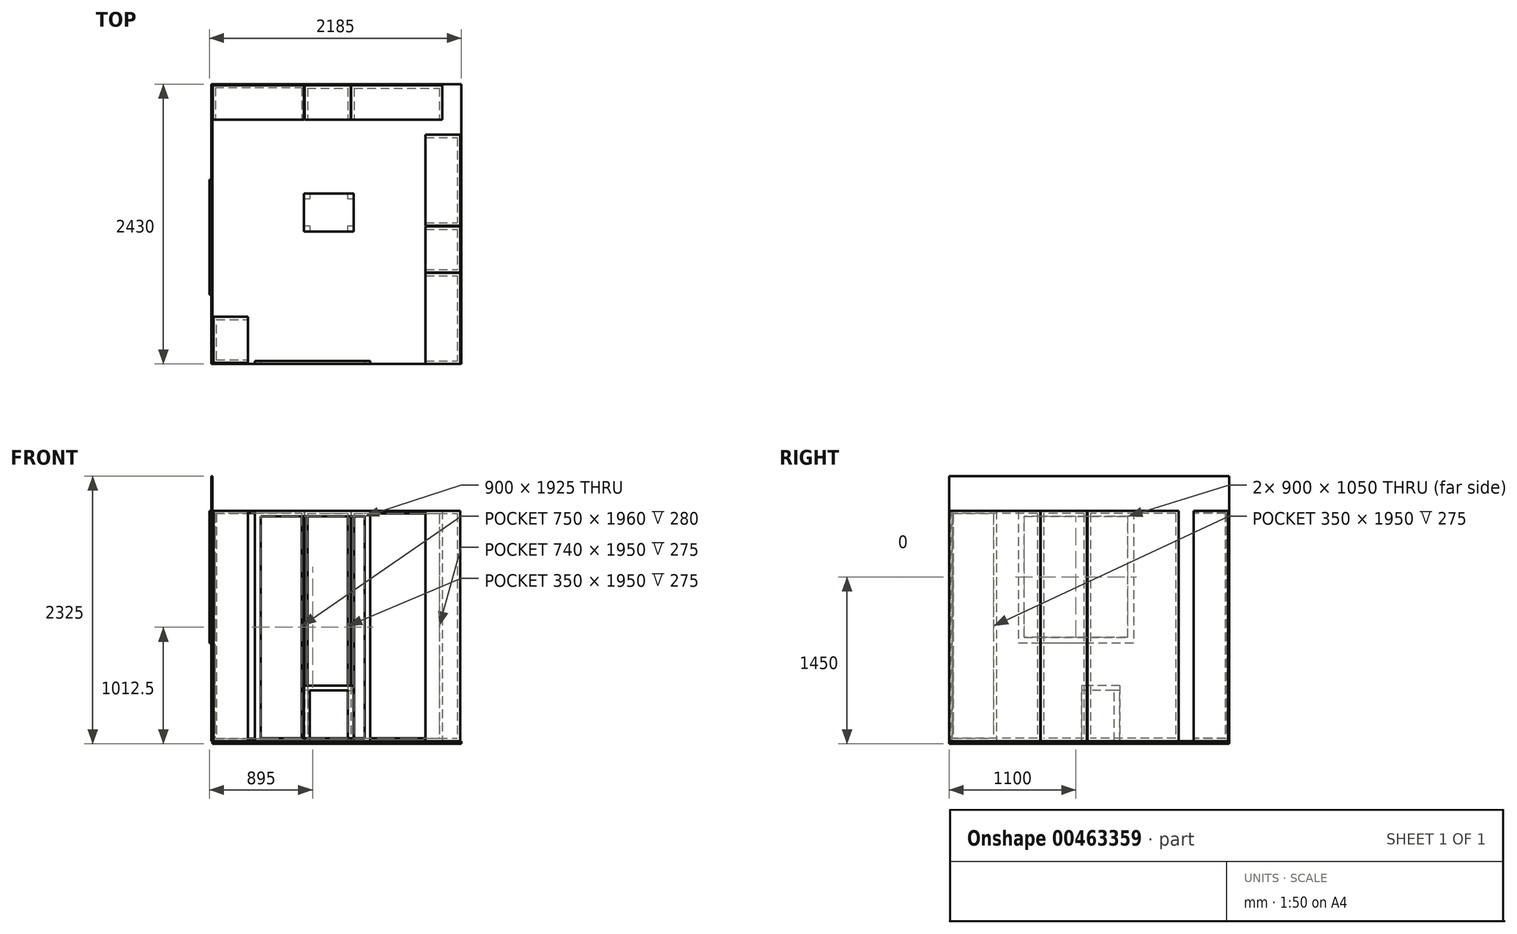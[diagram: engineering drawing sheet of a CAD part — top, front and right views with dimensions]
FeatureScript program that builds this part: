
annotation { "Feature Type Name" : "Feature", "Feature Type Description" : "" }
export const myFeature = defineFeature(function(context is Context, id is Id, definition is map)
    precondition{}
    {
        {
            var Q0;
            Q0=qCreatedBy(makeId("Top.planeOp"),FACE);
            var sketch = newSketch(context, id + "F0", { "sketchPlane" : qUnion([Q0])});
            skLineSegment(sketch, "E0.bottom", {"start": v(0, 0) * mm, "end": v(2160, 0) * mm});
            skLineSegment(sketch, "E0.top", {"start": v(0, 2430) * mm, "end": v(2160, 2430) * mm});
            skLineSegment(sketch, "E0.left", {"start": v(0, 0) * mm, "end": v(0, 2430) * mm});
            skLineSegment(sketch, "E0.right", {"start": v(2160, 0) * mm, "end": v(2160, 2430) * mm});
            skSolve(sketch);
        }
        {
            var Q0;
            Q0=qCreatedBy(makeId("Top.planeOp"),FACE);
            var sketch = newSketch(context, id + "F1", { "sketchPlane" : qUnion([Q0])});
            skLineSegment(sketch, "E1.bottom", {"start": v(1850, 1990) * mm, "end": v(2150, 1990) * mm});
            skLineSegment(sketch, "E1.top", {"start": v(1850, 1200) * mm, "end": v(2150, 1200) * mm});
            skLineSegment(sketch, "E1.left", {"start": v(1850, 1990) * mm, "end": v(1850, 1200) * mm});
            skLineSegment(sketch, "E1.right", {"start": v(2150, 1990) * mm, "end": v(2150, 1200) * mm});
            skPoint(sketch, "E2", {"position": v(1850, 1990) * mm});
            skSolve(sketch);
        }
        {
            var Q0;
            Q0=qCreatedBy(makeId("Top.planeOp"),FACE);
            var sketch = newSketch(context, id + "F2", { "sketchPlane" : qUnion([Q0])});
            skLineSegment(sketch, "E3.bottom", {"start": v(800, 2420) * mm, "end": v(1200, 2420) * mm});
            skLineSegment(sketch, "E3.top", {"start": v(800, 2120) * mm, "end": v(1200, 2120) * mm});
            skLineSegment(sketch, "E3.left", {"start": v(800, 2420) * mm, "end": v(800, 2120) * mm});
            skLineSegment(sketch, "E3.right", {"start": v(1200, 2420) * mm, "end": v(1200, 2120) * mm});
            skSolve(sketch);
        }
        {
            var Q0;
            Q0=qCreatedBy(makeId("Top.planeOp"),FACE);
            var sketch = newSketch(context, id + "F3", { "sketchPlane" : qUnion([Q0])});
            skLineSegment(sketch, "E4.bottom", {"start": v(5, 2420) * mm, "end": v(795, 2420) * mm});
            skLineSegment(sketch, "E4.top", {"start": v(5, 2120) * mm, "end": v(795, 2120) * mm});
            skLineSegment(sketch, "E4.left", {"start": v(5, 2420) * mm, "end": v(5, 2120) * mm});
            skLineSegment(sketch, "E4.right", {"start": v(795, 2420) * mm, "end": v(795, 2120) * mm});
            skSolve(sketch);
        }
        {
            var Q0;
            Q0 = qSketchRegion(id + "F3", true);
            extrude(context, id + "F4", {"entities" : qUnion([Q0]), "depth" : 2000 * mm});
        }
        {
            var Q0;
            Q0 = qSketchRegion(id + "F2", true);
            extrude(context, id + "F5", {"entities" : qUnion([Q0]), "depth" : 2000 * mm});
        }
        {
            var Q0;
            Q0 = qSketchRegion(id + "F1", true);
            extrude(context, id + "F6", {"entities" : qUnion([Q0]), "depth" : 2000 * mm});
        }
        {
            var Q0;
            Q0=qCreatedBy(makeId("Top.planeOp"),FACE);
            var sketch = newSketch(context, id + "F7", { "sketchPlane" : qUnion([Q0])});
            skLineSegment(sketch, "E5.bottom", {"start": v(1850, 1195) * mm, "end": v(2150, 1195) * mm});
            skLineSegment(sketch, "E5.top", {"start": v(1850, 795) * mm, "end": v(2150, 795) * mm});
            skLineSegment(sketch, "E5.left", {"start": v(1850, 1195) * mm, "end": v(1850, 795) * mm});
            skLineSegment(sketch, "E5.right", {"start": v(2150, 1195) * mm, "end": v(2150, 795) * mm});
            skSolve(sketch);
        }
        {
            var Q0;
            Q0 = qSketchRegion(id + "F7", true);
            extrude(context, id + "F8", {"entities" : qUnion([Q0]), "depth" : 2000 * mm});
        }
        {
            var Q0;
            Q0=qCreatedBy(makeId("Top.planeOp"),FACE);
            var sketch = newSketch(context, id + "F9", { "sketchPlane" : qUnion([Q0])});
            skLineSegment(sketch, "E6.bottom", {"start": v(1850, 790) * mm, "end": v(2150, 790) * mm});
            skLineSegment(sketch, "E6.top", {"start": v(1850, 0) * mm, "end": v(2150, 0) * mm});
            skLineSegment(sketch, "E6.left", {"start": v(1850, 790) * mm, "end": v(1850, 0) * mm});
            skLineSegment(sketch, "E6.right", {"start": v(2150, 790) * mm, "end": v(2150, 0) * mm});
            skSolve(sketch);
        }
        {
            var Q0;
            Q0 = qSketchRegion(id + "F9", true);
            extrude(context, id + "F10", {"entities" : qUnion([Q0]), "depth" : 2000 * mm});
        }
        {
            var Q0;
            Q0=makeQuery(id+"F4.opExtrude","SWEPT_FACE",FACE,{"disambiguationData":[OSD([sQuery(id+"F3.wireOp",EDGE,"E4.top")])]});
            shell(context, id + "F11", {"entities" : qUnion([Q0]), "thickness" : 20 * mm});
        }
        {
            var Q0;
            Q0=makeQuery(id+"F5.opExtrude","SWEPT_FACE",FACE,{"disambiguationData":[OSD([sQuery(id+"F2.wireOp",EDGE,"E3.top")])]});
            shell(context, id + "F12", {"entities" : qUnion([Q0]), "thickness" : 25 * mm});
        }
        {
            var Q0;
            Q0=qCreatedBy(makeId("Top.planeOp"),FACE);
            var sketch = newSketch(context, id + "F13", { "sketchPlane" : qUnion([Q0])});
            skLineSegment(sketch, "E7.bottom", {"start": v(10, 10) * mm, "end": v(310, 10) * mm});
            skLineSegment(sketch, "E7.top", {"start": v(10, 410) * mm, "end": v(310, 410) * mm});
            skLineSegment(sketch, "E7.left", {"start": v(10, 10) * mm, "end": v(10, 410) * mm});
            skLineSegment(sketch, "E7.right", {"start": v(310, 10) * mm, "end": v(310, 410) * mm});
            skSolve(sketch);
        }
        {
            var Q0;
            Q0 = qSketchRegion(id + "F13", true);
            extrude(context, id + "F14", {"entities" : qUnion([Q0]), "depth" : 2000 * mm});
        }
        {
            var Q0;
            Q0=makeQuery(id+"F14.opExtrude","SWEPT_FACE",FACE,{"disambiguationData":[OSD([sQuery(id+"F13.wireOp",EDGE,"E7.right")])]});
            shell(context, id + "F15", {"entities" : qUnion([Q0]), "thickness" : 25 * mm});
        }
        {
            var Q0;
            Q0=qCreatedBy(makeId("Front.planeOp"),FACE);
            var sketch = newSketch(context, id + "F16", { "sketchPlane" : qUnion([Q0])});
            skLineSegment(sketch, "E8.bottom", {"start": v(1370, 0) * mm, "end": v(370, 0) * mm});
            skLineSegment(sketch, "E8.top", {"start": v(1370, 2000) * mm, "end": v(370, 2000) * mm});
            skLineSegment(sketch, "E8.left", {"start": v(1370, 0) * mm, "end": v(1370, 2000) * mm});
            skLineSegment(sketch, "E8.right", {"start": v(370, 0) * mm, "end": v(370, 2000) * mm});
            skSolve(sketch);
        }
        {
            var Q0;
            Q0=makeQuery(id+"F0.imprint","IMPRINT",FACE,{"disambiguationData":[TD([[makeQuery(id+"F0.imprint","IMPRINT",EDGE,{"derivedFrom":sQuery(id+"F0.wireOp",EDGE,"E0.bottom")}),1.0]])]});
            var sketch = newSketch(context, id + "F17", { "sketchPlane" : qUnion([Q0])});
            skLineSegment(sketch, "E9.bottom", {"start": v(0, 2430) * mm, "end": v(-10, 2430) * mm});
            skLineSegment(sketch, "E9.top", {"start": v(0, 0) * mm, "end": v(-10, 0) * mm});
            skLineSegment(sketch, "E9.left", {"start": v(0, 2430) * mm, "end": v(0, 0) * mm});
            skLineSegment(sketch, "E9.right", {"start": v(-10, 2430) * mm, "end": v(-10, 0) * mm});
            skSolve(sketch);
        }
        {
            var Q0;
            Q0 = qSketchRegion(id + "F17", true);
            extrude(context, id + "F18", {"entities" : qUnion([Q0]), "depth" : 2300 * mm});
        }
        {
            var Q0;
            Q0 = qSketchRegion(id + "F16", true);
            extrude(context, id + "F19", {"entities" : qUnion([Q0]), "depth" : -25 * mm});
        }
        {
            var Q0;
            Q0=qCreatedBy(makeId("Right.planeOp"),FACE);
            var sketch = newSketch(context, id + "F20", { "sketchPlane" : qUnion([Q0])});
            skLineSegment(sketch, "E10.bottom", {"start": v(1600, 2000) * mm, "end": v(600, 2000) * mm});
            skLineSegment(sketch, "E10.top", {"start": v(1600, 850) * mm, "end": v(600, 850) * mm});
            skLineSegment(sketch, "E10.left", {"start": v(1600, 2000) * mm, "end": v(1600, 850) * mm});
            skLineSegment(sketch, "E10.right", {"start": v(600, 2000) * mm, "end": v(600, 850) * mm});
            skSolve(sketch);
        }
        {
            var Q0;
            Q0 = qSketchRegion(id + "F20", true);
            extrude(context, id + "F21", {"entities" : qUnion([Q0]), "depth" : -25 * mm});
        }
        {
            var Q0;
            Q0=makeQuery(id+"F19.opExtrude","CAP_FACE",FACE,{"disambiguationData":[OSD([sQuery(id+"F16.wireOp",EDGE,"E8.bottom"),sQuery(id+"F16.wireOp",EDGE,"E8.top"),sQuery(id+"F16.wireOp",EDGE,"E8.left"),sQuery(id+"F16.wireOp",EDGE,"E8.right")])],"isStart":true});
            var sketch = newSketch(context, id + "F22", { "sketchPlane" : qUnion([Q0])});
            skLineSegment(sketch, "E11.bottom", {"start": v(420, 1950) * mm, "end": v(1320, 1950) * mm});
            skLineSegment(sketch, "E11.top", {"start": v(420, 25) * mm, "end": v(1320, 25) * mm});
            skLineSegment(sketch, "E11.left", {"start": v(420, 1950) * mm, "end": v(420, 25) * mm});
            skLineSegment(sketch, "E11.right", {"start": v(1320, 1950) * mm, "end": v(1320, 25) * mm});
            skSolve(sketch);
        }
        {
            var Q0;
            Q0 = qSketchRegion(id + "F22", true);
            extrude(context, id + "F23", {"entities" : qUnion([Q0]), "operationType" : NewBodyOperationType.REMOVE, "oppositeDirection" : true, "depth" : 25 * mm});
        }
        {
            var Q0;
            Q0=makeQuery(id+"F21.opExtrude","CAP_FACE",FACE,{"disambiguationData":[OSD([sQuery(id+"F20.wireOp",EDGE,"E10.bottom"),sQuery(id+"F20.wireOp",EDGE,"E10.top"),sQuery(id+"F20.wireOp",EDGE,"E10.left"),sQuery(id+"F20.wireOp",EDGE,"E10.right")])],"isStart":false});
            var sketch = newSketch(context, id + "F24", { "sketchPlane" : qUnion([Q0])});
            skLineSegment(sketch, "E12.bottom", {"start": v(-1550, 1950) * mm, "end": v(-650, 1950) * mm});
            skLineSegment(sketch, "E12.top", {"start": v(-1550, 900) * mm, "end": v(-650, 900) * mm});
            skLineSegment(sketch, "E12.left", {"start": v(-1550, 1950) * mm, "end": v(-1550, 900) * mm});
            skLineSegment(sketch, "E12.right", {"start": v(-650, 1950) * mm, "end": v(-650, 900) * mm});
            skSolve(sketch);
        }
        {
            var Q0;
            Q0 = qSketchRegion(id + "F24", true);
            extrude(context, id + "F25", {"entities" : qUnion([Q0]), "operationType" : NewBodyOperationType.REMOVE, "endBound" : BoundingType.SYMMETRIC, "oppositeDirection" : true, "depth" : 50 * mm});
        }
        {
            var Q0;
            Q0=makeQuery(id+"F0.imprint","IMPRINT",FACE,{"disambiguationData":[TD([[makeQuery(id+"F0.imprint","IMPRINT",EDGE,{"derivedFrom":sQuery(id+"F0.wireOp",EDGE,"E0.bottom")}),1.0]])]});
            var sketch = newSketch(context, id + "F26", { "sketchPlane" : qUnion([Q0])});
            skLineSegment(sketch, "E13.left", {"start": v(1200, 2420) * mm, "end": v(1200, 2393.73) * mm});
            skLineSegment(sketch, "E14.bottom", {"start": v(1205, 2420) * mm, "end": v(1995, 2420) * mm});
            skLineSegment(sketch, "E14.top", {"start": v(1205, 2120) * mm, "end": v(1995, 2120) * mm});
            skLineSegment(sketch, "E14.left", {"start": v(1205, 2420) * mm, "end": v(1205, 2120) * mm});
            skLineSegment(sketch, "E14.right", {"start": v(1995, 2420) * mm, "end": v(1995, 2120) * mm});
            skSolve(sketch);
        }
        {
            var Q0;
            Q0 = qSketchRegion(id + "F26", true);
            extrude(context, id + "F27", {"entities" : qUnion([Q0]), "depth" : 2000 * mm});
        }
        {
            var Q0;
            Q0=makeQuery(id+"F27.opExtrude","SWEPT_FACE",FACE,{"disambiguationData":[OSD([sQuery(id+"F26.wireOp",EDGE,"E14.top")])]});
            shell(context, id + "F28", {"entities" : qUnion([Q0]), "thickness" : 25 * mm});
        }
        {
            var Q0;
            Q0=makeQuery(id+"F6.opExtrude","SWEPT_FACE",FACE,{"disambiguationData":[OSD([sQuery(id+"F1.wireOp",EDGE,"E1.left")])]});
            var Q1;
            Q1=makeQuery(id+"F8.opExtrude","SWEPT_FACE",FACE,{"disambiguationData":[OSD([sQuery(id+"F7.wireOp",EDGE,"E5.left")])]});
            var Q2;
            Q2=makeQuery(id+"F10.opExtrude","SWEPT_FACE",FACE,{"disambiguationData":[OSD([sQuery(id+"F9.wireOp",EDGE,"E6.left")])]});
            shell(context, id + "F29", {"entities" : qUnion([Q0, Q1, Q2]), "thickness" : 25 * mm});
        }
        {
            var Q0;
            Q0 = qSketchRegion(id + "F0", true);
            extrude(context, id + "F30", {"entities" : qUnion([Q0]), "depth" : -25 * mm});
        }
        {
            var Q0;
            Q0=makeQuery(id+"F0.imprint","IMPRINT",FACE,{"disambiguationData":[TD([[makeQuery(id+"F0.imprint","IMPRINT",EDGE,{"derivedFrom":sQuery(id+"F0.wireOp",EDGE,"E0.bottom")}),1.0]])]});
            var sketch = newSketch(context, id + "F31", { "sketchPlane" : qUnion([Q0])});
            skLineSegment(sketch, "E15.bottom", {"start": v(795.26, 1480.77) * mm, "end": v(1225.26, 1480.77) * mm});
            skLineSegment(sketch, "E15.top", {"start": v(795.26, 1150.77) * mm, "end": v(1225.26, 1150.77) * mm});
            skLineSegment(sketch, "E15.left", {"start": v(795.26, 1480.77) * mm, "end": v(795.26, 1150.77) * mm});
            skLineSegment(sketch, "E15.right", {"start": v(1225.26, 1480.77) * mm, "end": v(1225.26, 1150.77) * mm});
            skSolve(sketch);
        }
        {
            var Q0;
            Q0 = qSketchRegion(id + "F31", true);
            extrude(context, id + "F32", {"entities" : qUnion([Q0]), "operationType" : NewBodyOperationType.ADD, "depth" : 440 * mm});
        }
        {
            var Q0;
            Q0=makeQuery(id+"F32.opExtrude","CAP_FACE",FACE,{"disambiguationData":[OSD([sQuery(id+"F31.wireOp",EDGE,"E15.bottom"),sQuery(id+"F31.wireOp",EDGE,"E15.top"),sQuery(id+"F31.wireOp",EDGE,"E15.left"),sQuery(id+"F31.wireOp",EDGE,"E15.right")])],"isStart":false});
            var sketch = newSketch(context, id + "F33", { "sketchPlane" : qUnion([Q0])});
            skLineSegment(sketch, "E16", {"start": v(845.26, 1480.77) * mm, "end": v(845.26, 1430.77) * mm});
            skLineSegment(sketch, "E17", {"start": v(845.26, 1430.77) * mm, "end": v(795.26, 1430.77) * mm});
            skLineSegment(sketch, "E18", {"start": v(795.26, 1430.77) * mm, "end": v(795.26, 1200.77) * mm});
            skLineSegment(sketch, "E19", {"start": v(795.26, 1200.77) * mm, "end": v(845.26, 1200.77) * mm});
            skLineSegment(sketch, "E20", {"start": v(845.26, 1200.77) * mm, "end": v(845.26, 1150.77) * mm});
            skLineSegment(sketch, "E21", {"start": v(845.26, 1150.77) * mm, "end": v(1175.26, 1150.77) * mm});
            skLineSegment(sketch, "E22", {"start": v(1175.26, 1150.77) * mm, "end": v(1175.26, 1200.77) * mm});
            skLineSegment(sketch, "E23", {"start": v(1175.26, 1200.77) * mm, "end": v(1225.26, 1200.77) * mm});
            skLineSegment(sketch, "E24", {"start": v(1225.26, 1200.77) * mm, "end": v(1225.26, 1430.77) * mm});
            skLineSegment(sketch, "E25", {"start": v(1225.26, 1430.77) * mm, "end": v(1175.26, 1430.77) * mm});
            skLineSegment(sketch, "E26", {"start": v(1175.26, 1430.77) * mm, "end": v(1175.26, 1480.77) * mm});
            skLineSegment(sketch, "E27", {"start": v(1175.26, 1480.77) * mm, "end": v(845.26, 1480.77) * mm});
            skSolve(sketch);
        }
        {
            var Q0;
            Q0 = qSketchRegion(id + "F33", true);
            extrude(context, id + "F34", {"entities" : qUnion([Q0]), "operationType" : NewBodyOperationType.REMOVE, "oppositeDirection" : true, "depth" : 440 * mm});
        }
        {
            var Q0;
            {var subQ0=sQuery(id+"F31.wireOp",EDGE,"E15.bottom");var subQ1=sQuery(id+"F31.wireOp",EDGE,"E15.right");Q0=makeQuery(id+"F34.boolean.opBoolean","SPLIT",FACE,{"disambiguationData":[TD([makeQuery(id+"F34.opExtrude","SWEPT_FACE",FACE,{"disambiguationData":[OSD([sQuery(id+"F33.wireOp",EDGE,"E25")])]})])],"derivedFrom":makeQuery(id+"F32.opExtrude","CAP_FACE",FACE,{"disambiguationData":[OSD([subQ0,sQuery(id+"F31.wireOp",EDGE,"E15.top"),sQuery(id+"F31.wireOp",EDGE,"E15.left"),subQ1])],"isStart":false})});}
            var Q1;
            {var subQ0=sQuery(id+"F31.wireOp",EDGE,"E15.top");var subQ1=sQuery(id+"F31.wireOp",EDGE,"E15.left");Q1=makeQuery(id+"F34.boolean.opBoolean","SPLIT",FACE,{"disambiguationData":[TD([makeQuery(id+"F34.opExtrude","SWEPT_FACE",FACE,{"disambiguationData":[OSD([sQuery(id+"F33.wireOp",EDGE,"E19")])]})])],"derivedFrom":makeQuery(id+"F32.opExtrude","CAP_FACE",FACE,{"disambiguationData":[OSD([sQuery(id+"F31.wireOp",EDGE,"E15.bottom"),subQ0,subQ1,sQuery(id+"F31.wireOp",EDGE,"E15.right")])],"isStart":false})});}
            cPlane(context, id + "F35", {"entities" : qUnion([Q0, Q1]), "cplaneType" : CPlaneType.MID_PLANE, "offset" : 25 * mm, "width" : 150 * mm, "height" : 150 * mm});
        }
        {
            var Q0;
            Q0=qCreatedBy(id+"F35.planeOp",FACE);
            var sketch = newSketch(context, id + "F36", { "sketchPlane" : qUnion([Q0])});
            skLineSegment(sketch, "E28.bottom", {"start": v(795.26, 1480.77) * mm, "end": v(1225.26, 1480.77) * mm});
            skLineSegment(sketch, "E28.top", {"start": v(795.26, 1150.77) * mm, "end": v(1225.26, 1150.77) * mm});
            skLineSegment(sketch, "E28.left", {"start": v(795.26, 1480.77) * mm, "end": v(795.26, 1150.77) * mm});
            skLineSegment(sketch, "E28.right", {"start": v(1225.26, 1480.77) * mm, "end": v(1225.26, 1150.77) * mm});
            skSolve(sketch);
        }
        {
            var Q0;
            Q0 = qSketchRegion(id + "F36", true);
            extrude(context, id + "F37", {"entities" : qUnion([Q0]), "operationType" : NewBodyOperationType.ADD, "depth" : 40 * mm});
        }
    });
